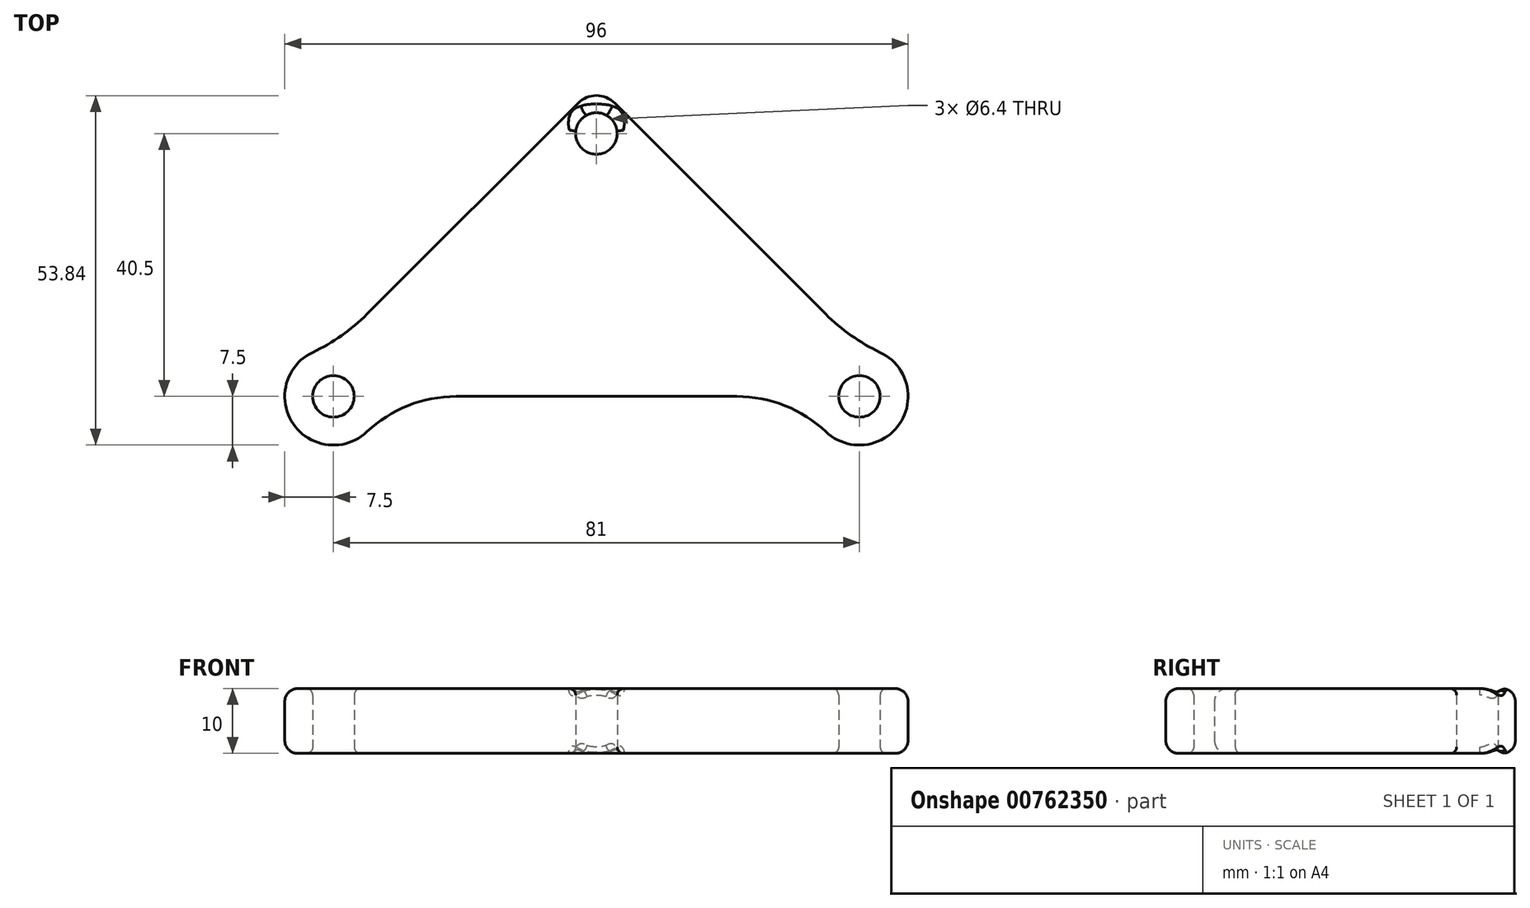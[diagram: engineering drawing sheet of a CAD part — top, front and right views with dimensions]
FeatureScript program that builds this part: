
annotation { "Feature Type Name" : "Feature", "Feature Type Description" : "" }
export const myFeature = defineFeature(function(context is Context, id is Id, definition is map)
    precondition{}
    {
        {
            var Q0;
            Q0=qCreatedBy(makeId("Top.planeOp"),FACE);
            var sketch = newSketch(context, id + "F0", { "sketchPlane" : qUnion([Q0])});
            skLineSegment(sketch, "E0", {"start": v(35.3, 12.7) * mm, "end": v(2.83, 45.17) * mm});
            skLineSegment(sketch, "E1", {"start": v(0, 0) * mm, "end": v(21.63, 0) * mm});
            skCircle(sketch, "E2", {"center": v(0, 40.5) * mm, "radius": 3.2 * mm});
            skCircle(sketch, "E3", {"center": v(40.5, 0) * mm, "radius": 3.2 * mm});
            skArc(sketch, "E4", {"start": v(35.35, -5.45) * mm, "mid": v(46.7, -4.23) * mm, "end": v(43.7, 6.78) * mm});
            skPoint(sketch, "E5.orphan", {"position": v(48, 0) * mm});
            skPoint(sketch, "E6.visualSharp", {"position": v(40.5, 7.5) * mm});
            skArc(sketch, "E6.filletArc", {"start": v(35.3, 12.7) * mm, "mid": v(39.25, 9.37) * mm, "end": v(43.7, 6.78) * mm});
            skPoint(sketch, "E7.visualSharp", {"position": v(33, 0) * mm});
            skArc(sketch, "E7.filletArc", {"start": v(35.35, -5.45) * mm, "mid": v(29.01, -1.41) * mm, "end": v(21.63, 0) * mm});
            skPoint(sketch, "E8.MirrorCS.end.orphan", {"position": v(0, 48) * mm});
            skPoint(sketch, "E9.orphan", {"position": v(0, 0) * mm});
            skLineSegment(sketch, "E10.MirrorCS", {"start": v(-35.3, 12.7) * mm, "end": v(-2.83, 45.17) * mm});
            skArc(sketch, "E11.MirrorCS", {"start": v(-35.3, 12.7) * mm, "mid": v(-39.25, 9.37) * mm, "end": v(-43.7, 6.78) * mm});
            skArc(sketch, "E12.MirrorCS", {"start": v(-35.35, -5.45) * mm, "mid": v(-46.7, -4.23) * mm, "end": v(-43.7, 6.78) * mm});
            skArc(sketch, "E13.MirrorCS", {"start": v(-35.35, -5.45) * mm, "mid": v(-29.01, -1.41) * mm, "end": v(-21.63, 0) * mm});
            skLineSegment(sketch, "E14.MirrorCS", {"start": v(0, 0) * mm, "end": v(-21.63, 0) * mm});
            skCircle(sketch, "E15.MirrorC", {"center": v(-40.5, 0) * mm, "radius": 3.2 * mm});
            skArc(sketch, "E16.filletArc", {"start": v(2.83, 45.17) * mm, "mid": v(0, 46.34) * mm, "end": v(-2.83, 45.17) * mm});
            skSolve(sketch);
        }
        {
            var Q0;
            Q0=makeQuery(id+"F0.imprint","IMPRINT",FACE,{"disambiguationData":[TD([[makeQuery(id+"F0.imprint","IMPRINT",EDGE,{"derivedFrom":sQuery(id+"F0.wireOp",EDGE,"E0")}),1.0]])]});
            extrude(context, id + "F1", {"entities" : qUnion([Q0]), "depth" : 10 * mm, "offsetDistance" : 25 * mm});
        }
        {
            var Q0;
            Q0=makeQuery(id+"F1.opExtrude","CAP_EDGE",EDGE,{"disambiguationData":[OSD([sQuery(id+"F0.wireOp",EDGE,"E1"),sQuery(id+"F0.wireOp",EDGE,"E14.MirrorCS")])],"isStart":true});
            var Q1;
            Q1=makeQuery(id+"F1.opExtrude","CAP_EDGE",EDGE,{"disambiguationData":[OSD([sQuery(id+"F0.wireOp",EDGE,"E7.filletArc")])],"isStart":true});
            fillet(context, id + "F2", {"entities" : qUnion([Q0, Q1]), "radius" : 2 * mm, "tangentPropagation" : true, "allowEdgeOverflow" : false});
        }
        {
            var Q0;
            Q0=makeQuery(id+"F1.opExtrude","CAP_EDGE",EDGE,{"disambiguationData":[OSD([sQuery(id+"F0.wireOp",EDGE,"E1"),sQuery(id+"F0.wireOp",EDGE,"E14.MirrorCS")])],"isStart":false});
            fillet(context, id + "F3", {"entities" : qUnion([Q0]), "radius" : 2 * mm, "tangentPropagation" : true, "allowEdgeOverflow" : false});
        }
        {
            var Q0;
            Q0=makeQuery(id+"F1.opExtrude","CAP_EDGE",EDGE,{"disambiguationData":[OSD([sQuery(id+"F0.wireOp",EDGE,"E15.MirrorC")])],"isStart":false});
            var Q1;
            Q1=makeQuery(id+"F1.opExtrude","CAP_EDGE",EDGE,{"disambiguationData":[OSD([sQuery(id+"F0.wireOp",EDGE,"E2")])],"isStart":false});
            var Q2;
            Q2=makeQuery(id+"F1.opExtrude","CAP_EDGE",EDGE,{"disambiguationData":[OSD([sQuery(id+"F0.wireOp",EDGE,"E3")])],"isStart":false});
            var Q3;
            Q3=makeQuery(id+"F1.opExtrude","CAP_EDGE",EDGE,{"disambiguationData":[OSD([sQuery(id+"F0.wireOp",EDGE,"E3")])],"isStart":true});
            var Q4;
            Q4=makeQuery(id+"F1.opExtrude","CAP_EDGE",EDGE,{"disambiguationData":[OSD([sQuery(id+"F0.wireOp",EDGE,"E2")])],"isStart":true});
            var Q5;
            Q5=makeQuery(id+"F1.opExtrude","CAP_EDGE",EDGE,{"disambiguationData":[OSD([sQuery(id+"F0.wireOp",EDGE,"E15.MirrorC")])],"isStart":true});
            fillet(context, id + "F4", {"entities" : qUnion([Q0, Q1, Q2, Q3, Q4, Q5]), "radius" : 1 * mm, "tangentPropagation" : true, "allowEdgeOverflow" : false});
        }
    });
